# Revit family: ADB Extra-wide gas range cookers L1000
name_source: partatom
category: Equipement spécialisé
units: mm (PartAtom-declared; Revit-internal decimal feet)

## family parameters
Basée sur le plan de construction = Non
Conserver l'orientation des annotations = Non
Cote de connecteur circulaire = Utiliser le diamètre
Couper avec des vides une fois chargée = Non
Numéro OmniClass = 23.40.40.14.17.11
Partagée = Non
Repère de localisation dans la pièce = Non
Titre OmniClass = Cookers, Ovens, Stoves
Toujours verticalement = Oui
Type d'élément = Normal

## types (2) — shared parameters
Commentaires du type = Ambassade range - Gas range cookers
Fabricant = Société Industrielle de Lacanche
Gas Size = 21 mm
Modèle = CG 1051 B
Pbase = 0 W
URL = https://www.ambassade-de-bourgogne.com
Weight = 128.00 kg
zero-valued in all types: Elévation par défaut

## per-type parameters (varying)
| type | Description | Electric power | Electrical Remarks | Gas Flow | Gas power kW | Pbase gaz |
| 5 Gas burners- 1 oven - CG 1051 B | Gas range cooker 5 Gas burners - 1 oven - CG 1051 B | 0 W | 230V(MONO) commutable 400V(TRI) | 0.8 L/s | 25.5 | 26 W |
| 5 Gas burners - 1 oven - option SFEB001_CG 1051 B | Gas range cooker 5 Gas burners - 1 oven - option SFEB001_CG 1051 B | 5000 W | 230V(MONO) commutable 400V(TRI), 400V TRI sans neutre en option | 0.5 L/s | 18.5 | 19 W |
